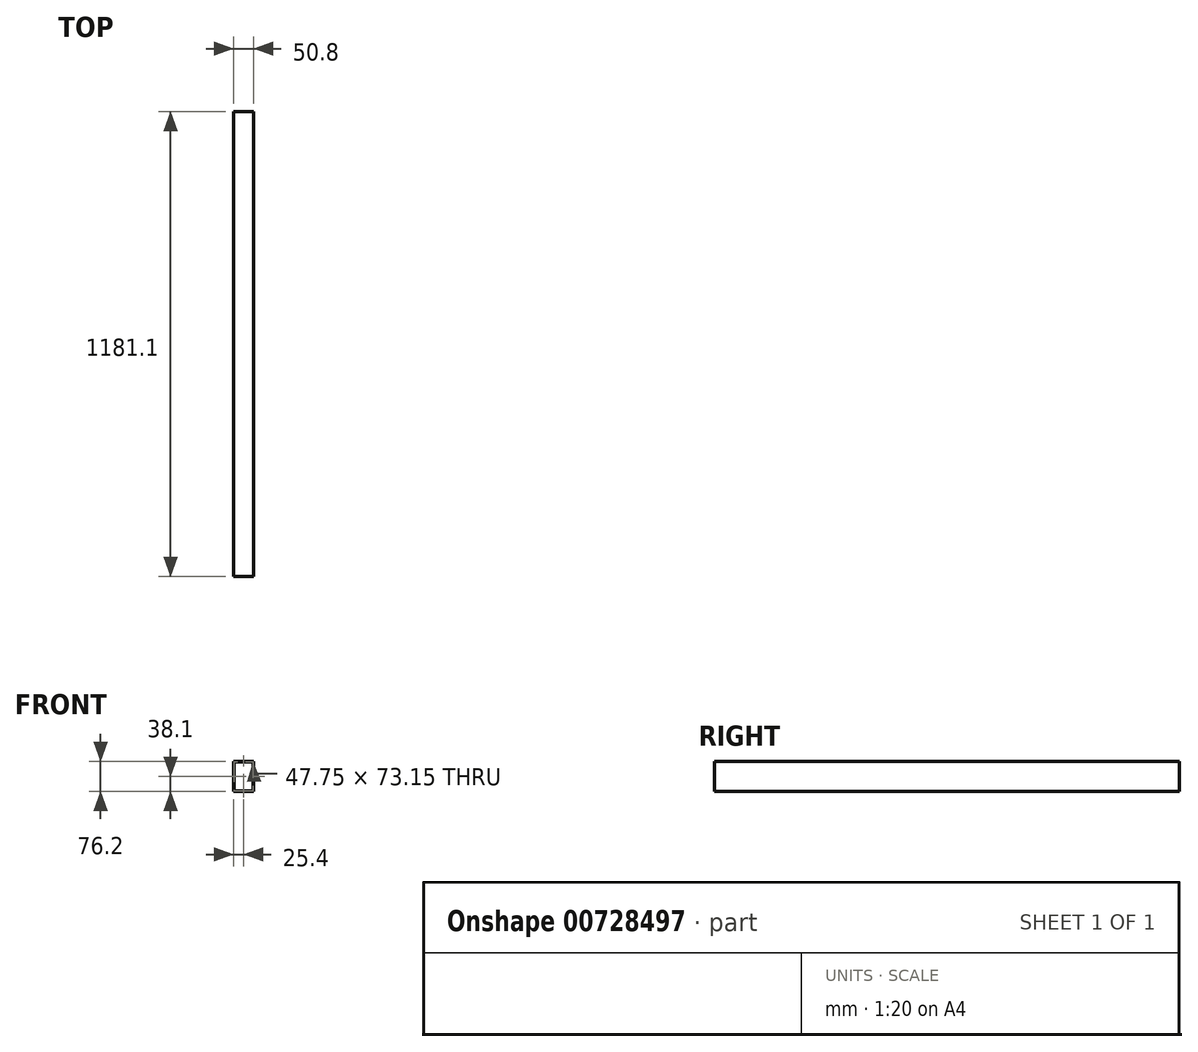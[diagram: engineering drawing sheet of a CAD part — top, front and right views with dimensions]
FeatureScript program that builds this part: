
annotation { "Feature Type Name" : "Feature", "Feature Type Description" : "" }
export const myFeature = defineFeature(function(context is Context, id is Id, definition is map)
    precondition{}
    {
        {
            var Q0;
            Q0=qCreatedBy(makeId("Front.planeOp"),FACE);
            var sketch = newSketch(context, id + "F0", { "sketchPlane" : qUnion([Q0])});
            skLineSegment(sketch, "E0.bottom", {"start": v(-25.4, 38.1) * mm, "end": v(25.4, 38.1) * mm});
            skLineSegment(sketch, "E0.top", {"start": v(-25.4, -38.1) * mm, "end": v(25.4, -38.1) * mm});
            skLineSegment(sketch, "E0.left", {"start": v(-25.4, 38.1) * mm, "end": v(-25.4, -38.1) * mm});
            skLineSegment(sketch, "E0.right", {"start": v(25.4, 38.1) * mm, "end": v(25.4, -38.1) * mm});
            skPoint(sketch, "E0.middle", {"position": v(0, 0) * mm});
            skLineSegment(sketch, "E1.bottom", {"start": v(-23.88, 36.58) * mm, "end": v(23.88, 36.58) * mm});
            skLineSegment(sketch, "E1.top", {"start": v(-23.88, -36.58) * mm, "end": v(23.88, -36.58) * mm});
            skLineSegment(sketch, "E1.left", {"start": v(-23.88, 36.58) * mm, "end": v(-23.88, -36.58) * mm});
            skLineSegment(sketch, "E1.right", {"start": v(23.88, 36.58) * mm, "end": v(23.88, -36.58) * mm});
            skSolve(sketch);
        }
        {
            var Q0;
            Q0=makeQuery(id+"F0.imprint","IMPRINT",FACE,{"disambiguationData":[TD([[makeQuery(id+"F0.imprint","IMPRINT",EDGE,{"derivedFrom":sQuery(id+"F0.wireOp",EDGE,"E0.bottom")}),-1.0]])]});
            extrude(context, id + "F1", {"entities" : qUnion([Q0]), "endBound" : BoundingType.SYMMETRIC, "depth" : 1181.1 * mm, "offsetDistance" : 25.4 * mm});
        }
    });
